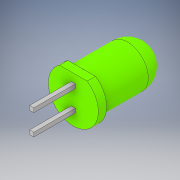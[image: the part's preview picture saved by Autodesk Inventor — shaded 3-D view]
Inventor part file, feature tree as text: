
AUTODESK INVENTOR PART (.ipt)
format: ipt  version: 2018 (Build 220112000, 112)  size: 154,112 bytes
history: native  units: mm
features: extrude x3, sketch x3, fillet x1
ambient origin geometry x8: Origin, YZ Plane, XZ Plane, XY Plane, X Axis, Y Axis, Z Axis, Center Point
bodies: Volumenkörper1 (feature_tree)
feature tree (7):
  extrude  "Höhe"  Depth=2.5mm TaperAngle=0.0deg
  fillet  "Radius_Kopf"  Radius=2.5mm
  extrude  "Kante"  Depth=1.0mm TaperAngle=0.0deg
  extrude  "Pin"  Depth=0.5mm
  sketch  "Skizze1"  dims[d0=5.0mm d1=8.0mm d2=0.0mm d3=2.5mm]
  sketch  "Skizze2"  dims[d4=6.0mm d5=1.0mm d6=0.0mm]
  sketch  "Skizze3"  dims[d7=2.54mm d8=0.5mm d9=0.5mm d10=5.0mm d11=0.0mm]
